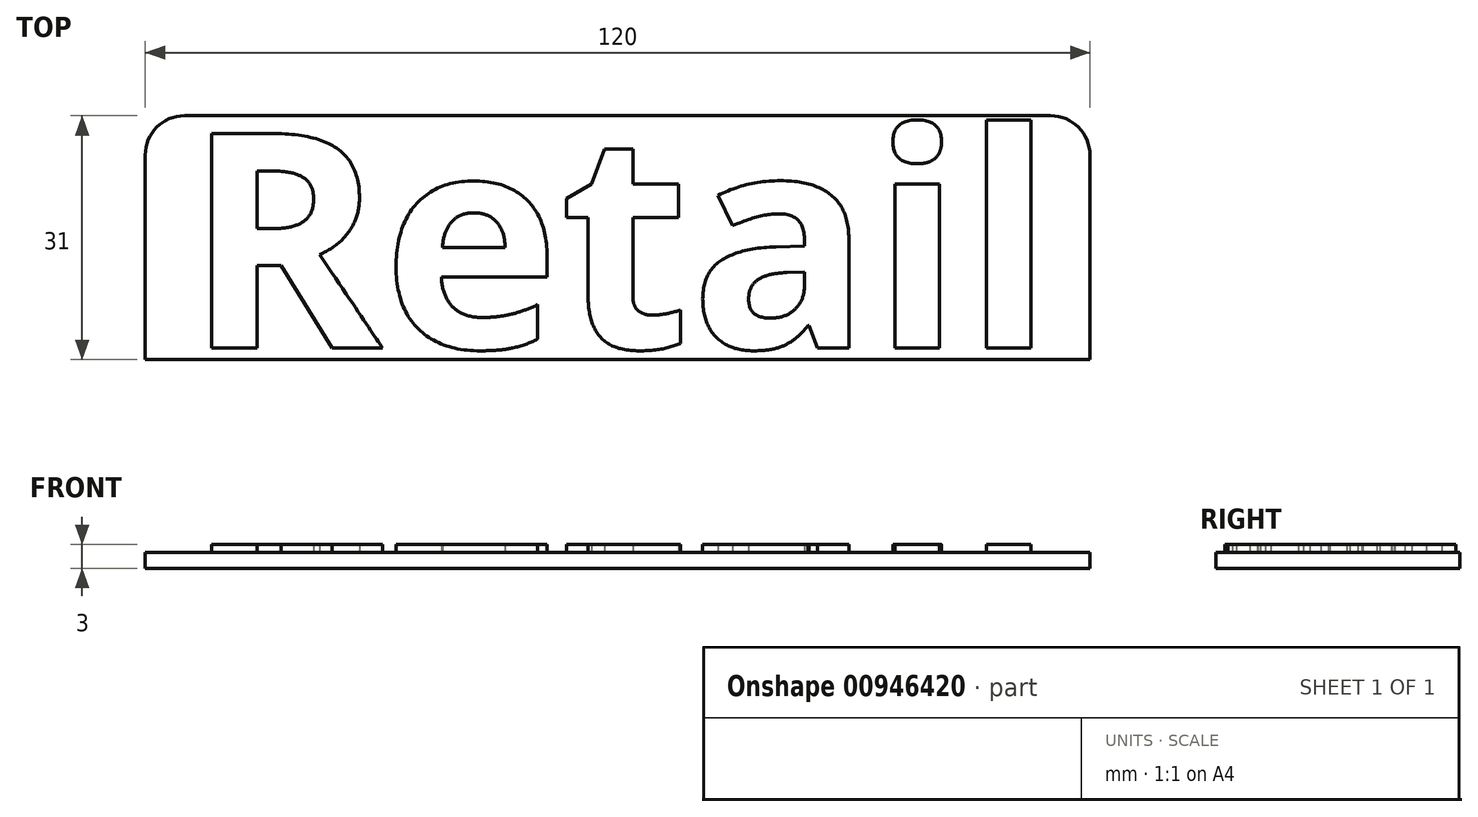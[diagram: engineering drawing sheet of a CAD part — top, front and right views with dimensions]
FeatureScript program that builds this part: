
annotation { "Feature Type Name" : "Feature", "Feature Type Description" : "" }
export const myFeature = defineFeature(function(context is Context, id is Id, definition is map)
    precondition{}
    {
        {
            var Q0;
            Q0=qCreatedBy(makeId("Top.planeOp"),FACE);
            var sketch = newSketch(context, id + "F0", { "sketchPlane" : qUnion([Q0])});
            skLineSegment(sketch, "E0.bottom", {"start": v(-60, 15.5) * mm, "end": v(60, 15.5) * mm});
            skLineSegment(sketch, "E0.top", {"start": v(-60, -15.5) * mm, "end": v(60, -15.5) * mm});
            skLineSegment(sketch, "E0.left", {"start": v(-60, 15.5) * mm, "end": v(-60, -15.5) * mm});
            skLineSegment(sketch, "E0.right", {"start": v(60, 15.5) * mm, "end": v(60, -15.5) * mm});
            skPoint(sketch, "E0.middle", {"position": v(0, 0) * mm});
            skSolve(sketch);
        }
        {
            var Q0;
            Q0=qSketchRegion(id+"F0",true);
            extrude(context, id + "F1", {"entities" : qUnion([Q0]), "depth" : 2 * mm, "offsetDistance" : 25 * mm});
        }
        {
            var Q0;
            Q0=makeQuery(id+"F1.opExtrude","CAP_FACE",FACE,{"disambiguationData":[OSD([sQuery(id+"F0.wireOp",EDGE,"E0.bottom"),sQuery(id+"F0.wireOp",EDGE,"E0.top"),sQuery(id+"F0.wireOp",EDGE,"E0.left"),sQuery(id+"F0.wireOp",EDGE,"E0.right")])],"isStart":false});
            var sketch = newSketch(context, id + "F2", { "sketchPlane" : qUnion([Q0])});
            skText(sketch, "E1", { "text": "Retail", "fontName": "OpenSans-Bold.ttf"});
            const initialGuessF2  = {"E1": [-0.055, -0.014, 1, 0, 0.02744]};
            skSetInitialGuess(sketch, initialGuessF2);
            skSolve(sketch);
        }
        {
            var Q0;
            Q0=qSketchRegion(id+"F2",true);
            extrude(context, id + "F3", {"entities" : qUnion([Q0]), "operationType" : NewBodyOperationType.ADD, "depth" : 1 * mm, "offsetDistance" : 25 * mm});
        }
        {
            var Q0;
            Q0=makeQuery(id+"F1.opExtrude","SWEPT_EDGE",EDGE,{"disambiguationData":[OSD([sQuery(id+"F0.wireOp",EDGE,"E0.bottom"),sQuery(id+"F0.wireOp",EDGE,"E0.left")])]});
            var Q1;
            Q1=makeQuery(id+"F1.opExtrude","SWEPT_EDGE",EDGE,{"disambiguationData":[OSD([sQuery(id+"F0.wireOp",EDGE,"E0.bottom"),sQuery(id+"F0.wireOp",EDGE,"E0.right")])]});
            fillet(context, id + "F4", {"entities" : qUnion([Q0, Q1]), "radius" : 5 * mm, "tangentPropagation" : true, "allowEdgeOverflow" : false});
        }
    });
